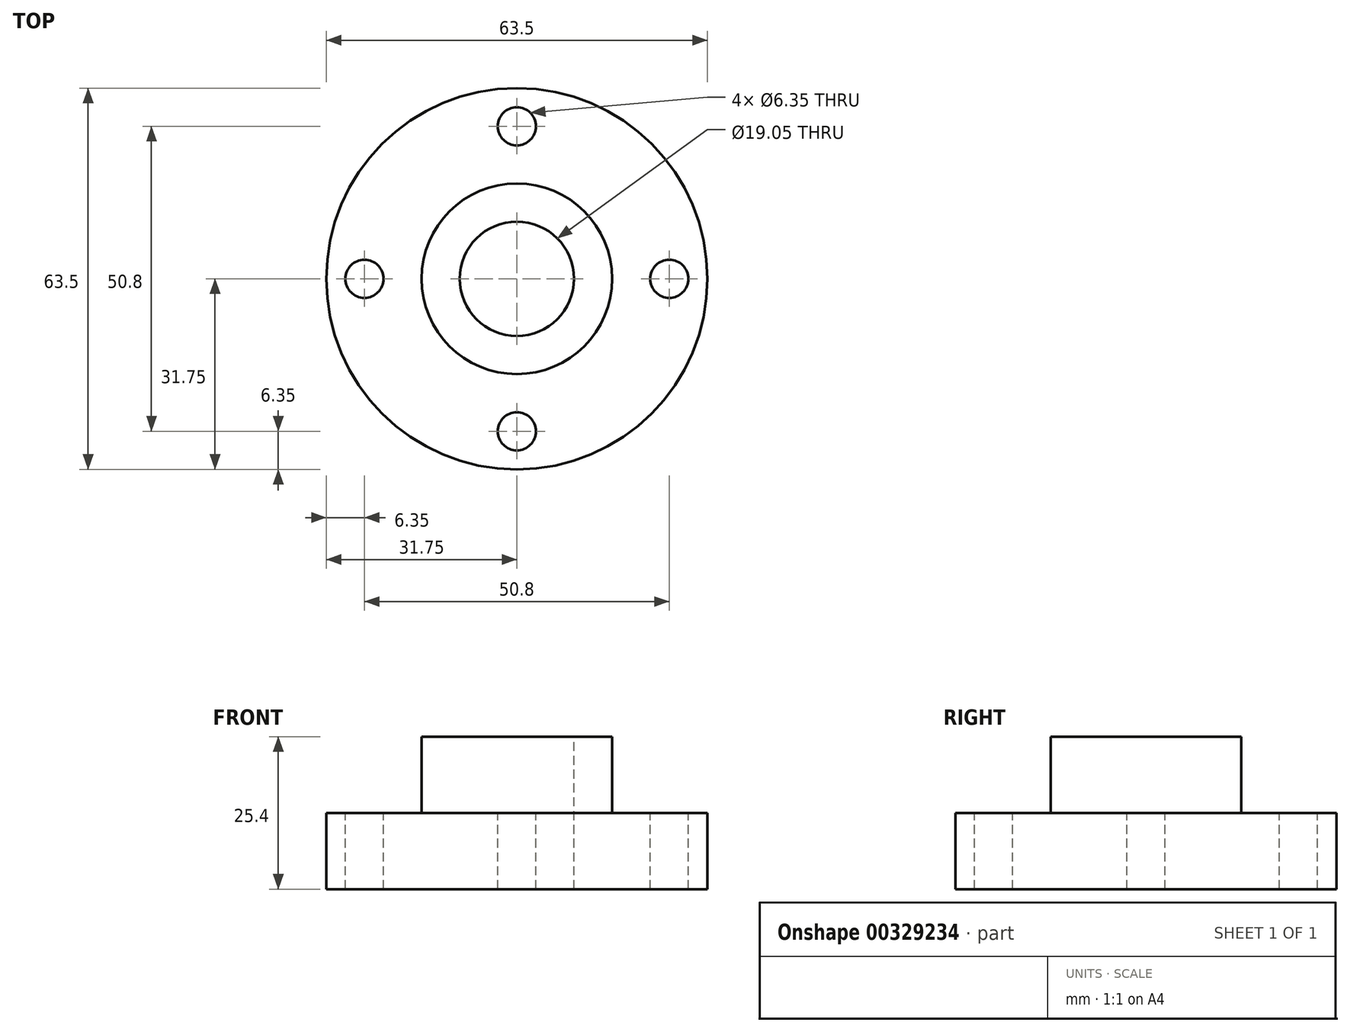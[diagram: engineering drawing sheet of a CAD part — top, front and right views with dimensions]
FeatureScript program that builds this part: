
annotation { "Feature Type Name" : "Feature", "Feature Type Description" : "" }
export const myFeature = defineFeature(function(context is Context, id is Id, definition is map)
    precondition{}
    {
        {
            var Q0;
            Q0=qCreatedBy(makeId("Top.planeOp"),FACE);
            var sketch = newSketch(context, id + "F0", { "sketchPlane" : qUnion([Q0])});
            skCircle(sketch, "E0", {"center": v(0, 0) * mm, "radius": 15.88 * mm});
            skCircle(sketch, "E1", {"center": v(0, 0) * mm, "radius": 31.75 * mm});
            skSolve(sketch);
        }
        {
            var Q0;
            Q0=makeQuery(id+"F0.imprint","IMPRINT",FACE,{"disambiguationData":[TD([[makeQuery(id+"F0.imprint","IMPRINT",EDGE,{"derivedFrom":sQuery(id+"F0.wireOp",EDGE,"E0")}),-1.0]])]});
            extrude(context, id + "F1", {"entities" : qUnion([Q0]), "depth" : 12.7 * mm});
        }
        {
            var Q0;
            Q0=makeQuery(id+"F0.imprint","IMPRINT",FACE,{"disambiguationData":[TD([[makeQuery(id+"F0.imprint","IMPRINT",EDGE,{"derivedFrom":sQuery(id+"F0.wireOp",EDGE,"E0")}),1.0]])]});
            extrude(context, id + "F2", {"entities" : qUnion([Q0]), "operationType" : NewBodyOperationType.ADD, "depth" : 25.4 * mm});
        }
        {
            var Q0;
            Q0=makeQuery(id+"F2.opExtrude","CAP_FACE",FACE,{"disambiguationData":[OSD([sQuery(id+"F0.wireOp",EDGE,"E0")])],"isStart":false});
            var sketch = newSketch(context, id + "F3", { "sketchPlane" : qUnion([Q0])});
            skCircle(sketch, "E2", {"center": v(0, 0) * mm, "radius": 9.52 * mm});
            skCircle(sketch, "E3", {"center": v(0, 25.4) * mm, "radius": 3.18 * mm});
            skCircle(sketch, "E4", {"center": v(25.4, 0) * mm, "radius": 3.18 * mm});
            skCircle(sketch, "E5", {"center": v(0, -25.4) * mm, "radius": 3.18 * mm});
            skCircle(sketch, "E6", {"center": v(-25.4, 0) * mm, "radius": 3.18 * mm});
            skSolve(sketch);
        }
        {
            var Q0;
            Q0 = qSketchRegion(id + "F3", true);
            extrude(context, id + "F4", {"entities" : qUnion([Q0]), "operationType" : NewBodyOperationType.REMOVE, "endBound" : BoundingType.THROUGH_ALL, "oppositeDirection" : true, "depth" : 25.4 * mm});
        }
    });
